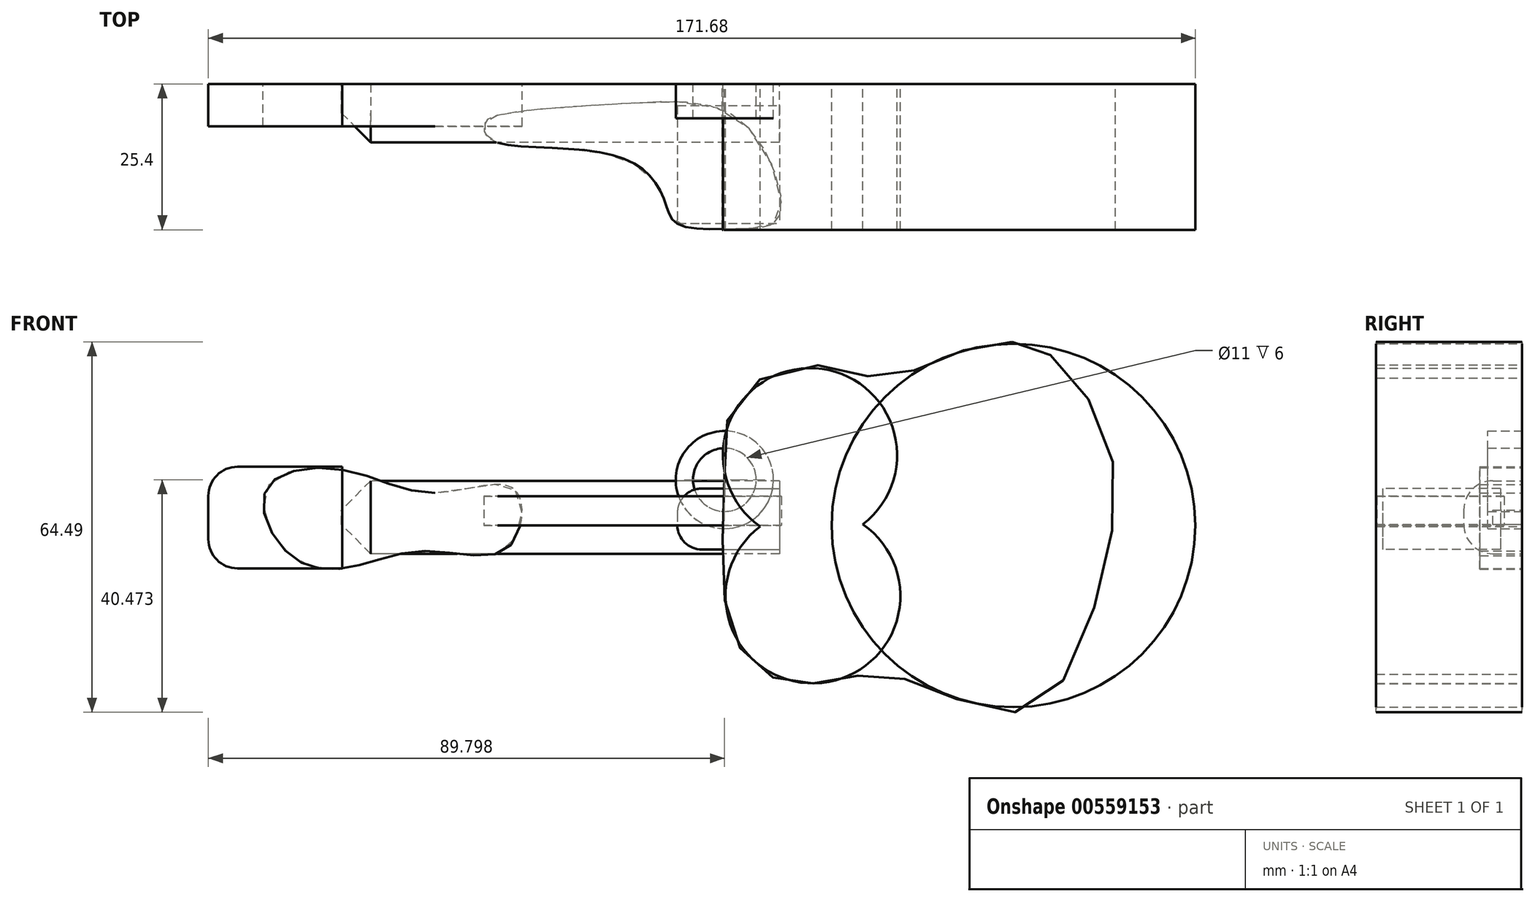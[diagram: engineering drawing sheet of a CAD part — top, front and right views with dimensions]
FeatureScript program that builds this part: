
annotation { "Feature Type Name" : "Feature", "Feature Type Description" : "" }
export const myFeature = defineFeature(function(context is Context, id is Id, definition is map)
    precondition{}
    {
        {
            var Q0;
            Q0=qCreatedBy(makeId("Front.planeOp"),FACE);
            var sketch = newSketch(context, id + "F0", { "sketchPlane" : qUnion([Q0])});
            skCircle(sketch, "E0", {"center": v(40.7, 0) * mm, "radius": 31.63 * mm});
            skSolve(sketch);
        }
        {
            var Q0;
            Q0=qCreatedBy(makeId("Front.planeOp"),FACE);
            var sketch = newSketch(context, id + "F1", { "sketchPlane" : qUnion([Q0])});
            skCircle(sketch, "E1", {"center": v(5.3, 12.26) * mm, "radius": 15.15 * mm});
            skCircle(sketch, "E2", {"center": v(5.81, -12.26) * mm, "radius": 15.2 * mm});
            skSolve(sketch);
        }
        {
            var Q0;
            Q0=qCreatedBy(makeId("Front.planeOp"),FACE);
            var sketch = newSketch(context, id + "F2", { "sketchPlane" : qUnion([Q0])});
            skFitSpline(sketch, "E3", {"points": [v(40.45, 31.98) * mm, v(29.07, 29.45) * mm, v(17.95, 25.66) * mm, v(6.57, 27.93) * mm, v(-7.33, 22.12) * mm, v(-9.6, 8.97) * mm, v(-9.86, -9.23) * mm, v(-6.83, -21.36) * mm, v(0, -26.92) * mm, v(7.84, -27.18) * mm, v(17.7, -25.91) * mm, v(29.58, -29.7) * mm, v(44.74, -31.47) * mm, v(56.12, -9.23) * mm, v(57.38, 13.78) * mm, v(47.78, 29.2) * mm, v(40.45, 31.98) * mm]});
            skSolve(sketch);
        }
        {
            var Q0;
            Q0=qCreatedBy(makeId("Front.planeOp"),FACE);
            var sketch = newSketch(context, id + "F3", { "sketchPlane" : qUnion([Q0])});
            skLineSegment(sketch, "E4.bottom", {"start": v(0, 7.8) * mm, "end": v(-76.2, 7.8) * mm});
            skLineSegment(sketch, "E4.top", {"start": v(0, -4.9) * mm, "end": v(-76.2, -4.9) * mm});
            skLineSegment(sketch, "E4.left", {"start": v(0, 7.8) * mm, "end": v(0, -4.9) * mm});
            skLineSegment(sketch, "E4.right", {"start": v(-76.2, 7.8) * mm, "end": v(-76.2, -4.9) * mm});
            skSolve(sketch);
        }
        {
            var Q0;
            Q0=makeQuery(id+"F3.imprint","IMPRINT",FACE,{"disambiguationData":[TD([[makeQuery(id+"F3.imprint","IMPRINT",EDGE,{"derivedFrom":sQuery(id+"F3.wireOp",EDGE,"E4.bottom")}),1.0]])]});
            extrude(context, id + "F4", {"entities" : qUnion([Q0]), "depth" : 10.16 * mm, "offsetDistance" : 25.4 * mm});
        }
        {
            var Q0;
            Q0=makeQuery(id+"F4.opExtrude","CAP_EDGE",EDGE,{"disambiguationData":[OSD([sQuery(id+"F3.wireOp",EDGE,"E4.bottom")])],"isStart":false});
            var Q1;
            Q1=makeQuery(id+"F4.opExtrude","CAP_EDGE",EDGE,{"disambiguationData":[OSD([sQuery(id+"F3.wireOp",EDGE,"E4.top")])],"isStart":false});
            fillet(context, id + "F5", {"entities" : qUnion([Q0, Q1]), "radius" : 5.08 * mm, "tangentPropagation" : true, "allowEdgeOverflow" : false});
        }
        {
            var Q0;
            Q0=qCreatedBy(makeId("Right.planeOp"),FACE);
            var sketch = newSketch(context, id + "F6", { "sketchPlane" : qUnion([Q0])});
            skLineSegment(sketch, "E5.bottom", {"start": v(-3.8, 6.45) * mm, "end": v(-24.27, 6.45) * mm});
            skLineSegment(sketch, "E5.top", {"start": v(-3.8, -4.17) * mm, "end": v(-24.27, -4.17) * mm});
            skLineSegment(sketch, "E5.left", {"start": v(-3.8, 6.45) * mm, "end": v(-3.8, -4.17) * mm});
            skLineSegment(sketch, "E5.right", {"start": v(-24.27, 6.45) * mm, "end": v(-24.27, -4.17) * mm});
            skSolve(sketch);
        }
        {
            var Q0;
            Q0 = qSketchRegion(id + "F6", true);
            extrude(context, id + "F7", {"entities" : qUnion([Q0]), "oppositeDirection" : true, "depth" : 17.78 * mm, "offsetDistance" : 25.4 * mm});
        }
        {
            var Q0;
            Q0=makeQuery(id+"F7.opExtrude","CAP_EDGE",EDGE,{"disambiguationData":[OSD([sQuery(id+"F6.wireOp",EDGE,"E5.bottom")])],"isStart":false});
            var Q1;
            Q1=makeQuery(id+"F7.opExtrude","CAP_EDGE",EDGE,{"disambiguationData":[OSD([sQuery(id+"F6.wireOp",EDGE,"E5.top")])],"isStart":false});
            fillet(context, id + "F8", {"entities" : qUnion([Q0, Q1]), "radius" : 4.3 * mm, "tangentPropagation" : true, "allowEdgeOverflow" : false});
        }
        {
            var Q0;
            Q0=qCreatedBy(makeId("Top.planeOp"),FACE);
            var sketch = newSketch(context, id + "F9", { "sketchPlane" : qUnion([Q0])});
            skFitSpline(sketch, "E6", {"points": [v(-49.04, -10.24) * mm, v(-32.1, -11.76) * mm, v(-22.75, -15.8) * mm, v(-19.72, -21.1) * mm, v(-17.7, -24.4) * mm, v(-6.32, -25.15) * mm, v(0, -23.13) * mm, v(-5.81, -7.2) * mm, v(-26.54, -3.41) * mm, v(-49.8, -5.69) * mm, v(-51.32, -6.95) * mm, v(-51.32, -8.47) * mm, v(-49.04, -10.24) * mm]});
            skSolve(sketch);
        }
        {
            var Q0;
            Q0 = qSketchRegion(id + "F9", true);
            extrude(context, id + "F10", {"entities" : qUnion([Q0]), "depth" : 5.08 * mm, "offsetDistance" : 25.4 * mm});
        }
        {
            var Q0;
            Q0=qCreatedBy(makeId("Front.planeOp"),FACE);
            var sketch = newSketch(context, id + "F11", { "sketchPlane" : qUnion([Q0])});
            skLineSegment(sketch, "E7.bottom", {"start": v(-76.1, 10.24) * mm, "end": v(-99.35, 10.24) * mm});
            skLineSegment(sketch, "E7.top", {"start": v(-76.1, -7.46) * mm, "end": v(-99.35, -7.46) * mm});
            skLineSegment(sketch, "E7.left", {"start": v(-76.1, 10.24) * mm, "end": v(-76.1, -7.46) * mm});
            skLineSegment(sketch, "E7.right", {"start": v(-99.35, 10.24) * mm, "end": v(-99.35, -7.46) * mm});
            skSolve(sketch);
        }
        {
            var Q0;
            Q0 = qSketchRegion(id + "F2", true);
            var Q1;
            Q1 = qSketchRegion(id + "F1", true);
            var Q2;
            Q2 = qSketchRegion(id + "F0", true);
            extrude(context, id + "F12", {"entities" : qUnion([Q0, Q1, Q2]), "depth" : 25.4 * mm, "offsetDistance" : 25.4 * mm});
        }
        {
            var Q0;
            Q0=qCreatedBy(makeId("Front.planeOp"),FACE);
            var sketch = newSketch(context, id + "F13", { "sketchPlane" : qUnion([Q0])});
            skFitSpline(sketch, "E8", {"points": [v(-59.91, 5.69) * mm, v(-76.1, 9.73) * mm, v(-89.24, 6.45) * mm, v(-85.95, -4.42) * mm, v(-75.84, -7.46) * mm, v(-61.68, -4.42) * mm, v(-47.27, -3.92) * mm, v(-46, 6.2) * mm, v(-59.91, 5.69) * mm]});
            skSolve(sketch);
        }
        {
            var Q0;
            Q0 = qSketchRegion(id + "F11", true);
            var Q1;
            Q1 = qSketchRegion(id + "F13", true);
            extrude(context, id + "F14", {"entities" : qUnion([Q0, Q1]), "depth" : 7.37 * mm, "offsetDistance" : 25.4 * mm});
        }
        {
            var Q0;
            Q0=makeQuery(id+"F14.opExtrude","SWEPT_EDGE",EDGE,{"disambiguationData":[OSD([sQuery(id+"F11.wireOp",EDGE,"E7.bottom"),sQuery(id+"F11.wireOp",EDGE,"E7.right")])]});
            var Q1;
            Q1=makeQuery(id+"F14.opExtrude","SWEPT_EDGE",EDGE,{"disambiguationData":[OSD([sQuery(id+"F11.wireOp",EDGE,"E7.top"),sQuery(id+"F11.wireOp",EDGE,"E7.right")])]});
            fillet(context, id + "F15", {"entities" : qUnion([Q0, Q1]), "radius" : 5.08 * mm, "tangentPropagation" : true, "allowEdgeOverflow" : false});
        }
        {
            var Q0;
            Q0=makeQuery(id+"F4.opExtrude","CAP_EDGE",EDGE,{"disambiguationData":[OSD([sQuery(id+"F3.wireOp",EDGE,"E4.right")])],"isStart":false});
            chamfer(context, id + "F16", {"entities" : qUnion([Q0]), "width" : 5.08 * mm, "tangentPropagation" : true});
        }
        {
            var Q0;
            Q0=qCreatedBy(makeId("Front.planeOp"),FACE);
            var sketch = newSketch(context, id + "F17", { "sketchPlane" : qUnion([Q0])});
            skCircle(sketch, "E9", {"center": v(-9.55, 7.96) * mm, "radius": 5.5 * mm});
            skCircle(sketch, "E10", {"center": v(-9.55, 7.96) * mm, "radius": 8.5 * mm});
            skSolve(sketch);
        }
        {
            var Q0;
            Q0 = qSketchRegion(id + "F17", true);
            extrude(context, id + "F18", {"entities" : qUnion([Q0]), "depth" : 6 * mm, "offsetDistance" : 25.4 * mm});
        }
    });
